# Revit family: Sanitary_Accessories_Ponte-Giulio_Towel-holder-frame
name_source: partatom
category: Furniture
units: mm (PartAtom-declared; Revit-internal decimal feet)

## family parameters
Always vertical = No
Cut with Voids When Loaded = No
OmniClass Number = 23.40.20.00
OmniClass Title = General Furniture and Specialties
Room Calculation Point = No
Shared = No
Work Plane-Based = Yes

## types (1)
- Towel holder frame
    BIMobject category = Accessories
    BIMobject category code = sanitary-accessories1
    BIMobject main category = Sanitary
    BIMobject main category code = sanitary
    BOSUseNativeGeometries = 1
    Brand url = http://www.pontegiulio.com
    Default Elevation = 1219 mm
    Design country = United States
    Edition number = 1
    IFC Classification = Furniture
    Manufacturer country = China
    Manufacturer name = Ponte Giulio
    Material main = Stainless steel
    Product Guid = 995d8297-5747-4f0a-8577-be7b9790ab52
    Product SKU = F47APS05
    Product data url = https://bimobject.com
    Product family = Safe bathroom
    Product group = Bathroom accessories
    Product name = Towel holder frame
    Product url = https://www.pontegiulio.com
    QR code = http://bimobject.com
    Technical description = http://www.pgdb.it
    UNSPSC Code = 56
    Uniclass 1.4 Code = L824
    Uniclass 1.4 Description = Bathroom, toilet furniture and fittings

## geometry (parser evidence)
native form markers: Sweep x4
no freeform markers — native parametric forms only
